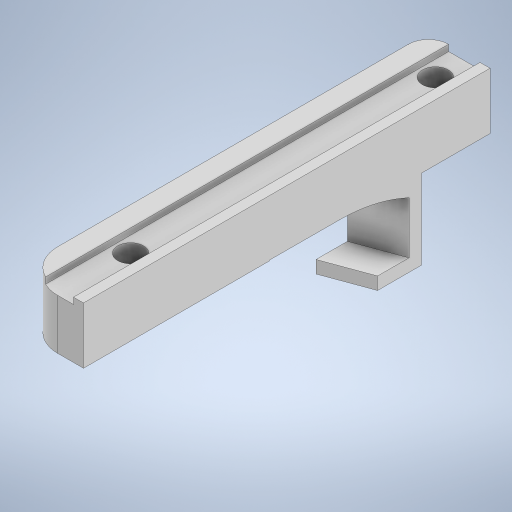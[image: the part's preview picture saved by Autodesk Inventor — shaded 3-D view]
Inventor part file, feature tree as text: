
AUTODESK INVENTOR PART (.ipt)
format: ipt  version: 2024 (Build 280153000, 153)  size: 329,216 bytes
history: native  units: in
note: dims shown in document units (in); Inventor stores cm internally (conversion verified against a paired STEP export)
features: extrude x7, sketch x4, plane x2
ambient origin geometry x8: Origin, YZ Plane, XZ Plane, XY Plane, X Axis, Y Axis, Z Axis, Center Point
bodies: Solid1 (feature_tree)
feature tree (13):
  sketch  "Sketch1"  dims[d0=0.126in d1=0.1614in]
  extrude  "Extrusion1"  Depth=0.126in
  extrude  "Extrusion3"  Depth=0.3937in
  extrude  "Extrusion2"  Depth=0.1181in
  sketch  "Sketch2"  dims[d2=2.3622in d4=0.3819in d5=0.3937in d7=0.3937in d9=0.2559in]
  plane  "Work Plane1"
  sketch  "Sketch3"  dims[d10=0.3937in d11=0.1181in]
  extrude  "Extrusion4"  Depth=0.126in
  extrude  "Extrusion5"  Depth=0.1969in
  plane  "Work Plane2"
  extrude  "Extrusion6"  Depth=0.2362in TaperAngle=0.0deg
  extrude  "Extrusion7"  Depth=0.1181in TaperAngle=0.0deg
  sketch  "Sketch4"  dims[d12=0.0354in d13=0.126in d14=0.2874in d15=0.2362in d16=0.0in d17=0.1181in d18=0.0in d19=0.1969in d20=0.0in d21=0.874in d22=0.0984in d23=0.0945in d24=15.0deg d25=0.3858in d26=0.0787in d27=0.315in d28=0.0787in d29=0.0in d30=0.874in d31=0.0in d32=0.0945in d33=0.0in d34=0.0in d35=0.1969in d36=0.0in d39=1.9094in]
